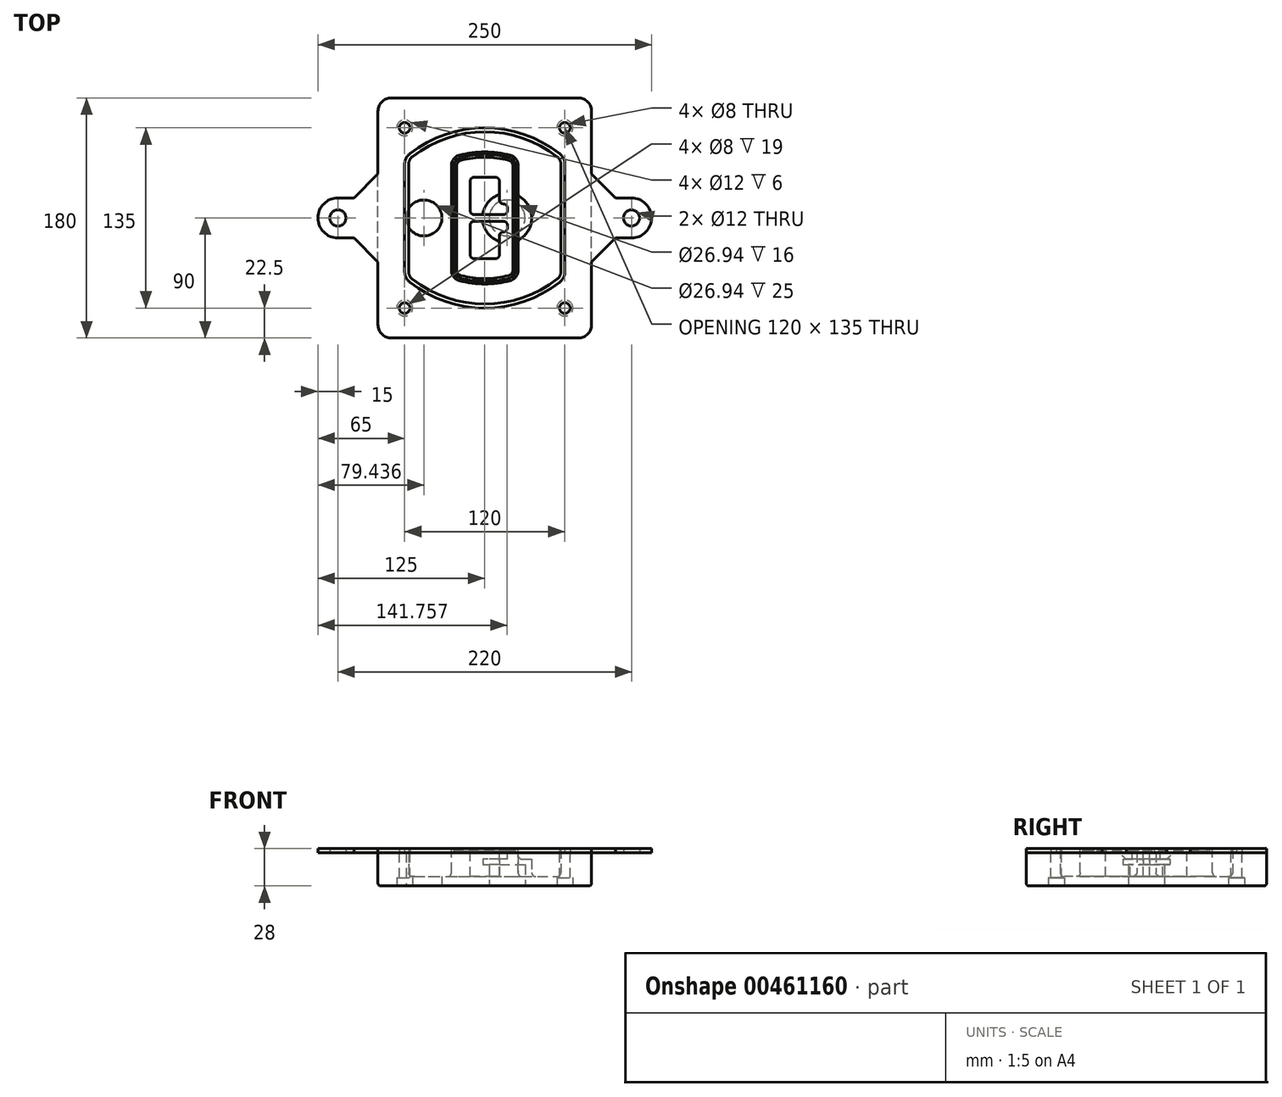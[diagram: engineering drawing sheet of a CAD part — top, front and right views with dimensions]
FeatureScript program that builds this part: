
annotation { "Feature Type Name" : "Feature", "Feature Type Description" : "" }
export const myFeature = defineFeature(function(context is Context, id is Id, definition is map)
    precondition{}
    {
        {
            var Q0;
            Q0=qCreatedBy(makeId("Top.planeOp"),FACE);
            var sketch = newSketch(context, id + "F0", { "sketchPlane" : qUnion([Q0])});
            skPoint(sketch, "E0.rect.middle", {"position": v(0, 0) * mm});
            skLineSegment(sketch, "E1.bottom", {"start": v(-70, -90) * mm, "end": v(70, -90) * mm});
            skLineSegment(sketch, "E1.top", {"start": v(-70, 90) * mm, "end": v(70, 90) * mm});
            skLineSegment(sketch, "E1.left", {"start": v(-80, -80) * mm, "end": v(-80, 80) * mm});
            skLineSegment(sketch, "E1.right", {"start": v(80, -80) * mm, "end": v(80, 80) * mm});
            skLineSegment(sketch, "E2", {"start": v(-80, 90) * mm, "end": v(80, -90) * mm, "construction": true});
            skLineSegment(sketch, "E3", {"start": v(80, 90) * mm, "end": v(-80, -90) * mm, "construction": true});
            skCircle(sketch, "E4", {"center": v(-60, 67.5) * mm, "radius": 4 * mm});
            skCircle(sketch, "E5", {"center": v(60, 67.5) * mm, "radius": 4 * mm});
            skCircle(sketch, "E6", {"center": v(60, -67.5) * mm, "radius": 4 * mm});
            skCircle(sketch, "E7", {"center": v(-60, -67.5) * mm, "radius": 4 * mm});
            skLineSegment(sketch, "E8", {"start": v(-60, 67.5) * mm, "end": v(60, 67.5) * mm, "construction": true});
            skLineSegment(sketch, "E9", {"start": v(60, 67.5) * mm, "end": v(60, -67.5) * mm, "construction": true});
            skLineSegment(sketch, "E10", {"start": v(60, -67.5) * mm, "end": v(-60, -67.5) * mm, "construction": true});
            skLineSegment(sketch, "E11", {"start": v(-60, -67.5) * mm, "end": v(-60, 67.5) * mm, "construction": true});
            skLineSegment(sketch, "E12", {"start": v(-60, 40.3) * mm, "end": v(-60, -40.3) * mm});
            skLineSegment(sketch, "E13", {"start": v(60, 40.3) * mm, "end": v(60, -40.3) * mm});
            skArc(sketch, "E14", {"start": v(56.15, 48.18) * mm, "mid": v(0, 67.5) * mm, "end": v(-56.15, 48.18) * mm});
            skArc(sketch, "E15", {"start": v(-56.15, -48.18) * mm, "mid": v(0, -67.5) * mm, "end": v(56.15, -48.18) * mm});
            skLineSegment(sketch, "E16", {"start": v(-60, 0) * mm, "end": v(60, 0) * mm, "construction": true});
            skPoint(sketch, "E17.visualSharp", {"position": v(-60, -45) * mm});
            skArc(sketch, "E17.filletArc", {"start": v(-60, -40.3) * mm, "mid": v(-58.99, -44.68) * mm, "end": v(-56.15, -48.18) * mm});
            skPoint(sketch, "E18.visualSharp", {"position": v(-60, 45) * mm});
            skArc(sketch, "E18.filletArc", {"start": v(-56.15, 48.18) * mm, "mid": v(-58.99, 44.68) * mm, "end": v(-60, 40.3) * mm});
            skPoint(sketch, "E19.visualSharp", {"position": v(60, 45) * mm});
            skArc(sketch, "E19.filletArc", {"start": v(60, 40.3) * mm, "mid": v(58.99, 44.68) * mm, "end": v(56.15, 48.18) * mm});
            skPoint(sketch, "E20.visualSharp", {"position": v(60, -45) * mm});
            skArc(sketch, "E20.filletArc", {"start": v(56.15, -48.18) * mm, "mid": v(58.99, -44.68) * mm, "end": v(60, -40.3) * mm});
            skPoint(sketch, "E21.visualSharp", {"position": v(-80, 90) * mm});
            skArc(sketch, "E21.filletArc", {"start": v(-70, 90) * mm, "mid": v(-77.07, 87.07) * mm, "end": v(-80, 80) * mm});
            skPoint(sketch, "E22.visualSharp", {"position": v(80, 90) * mm});
            skArc(sketch, "E22.filletArc", {"start": v(80, 80) * mm, "mid": v(77.07, 87.07) * mm, "end": v(70, 90) * mm});
            skPoint(sketch, "E23.visualSharp", {"position": v(80, -90) * mm});
            skArc(sketch, "E23.filletArc", {"start": v(70, -90) * mm, "mid": v(77.07, -87.07) * mm, "end": v(80, -80) * mm});
            skPoint(sketch, "E24.visualSharp", {"position": v(-80, -90) * mm});
            skArc(sketch, "E24.filletArc", {"start": v(-80, -80) * mm, "mid": v(-77.07, -87.07) * mm, "end": v(-70, -90) * mm});
            skArc(sketch, "E25.0", {"start": v(57, 40.3) * mm, "mid": v(56.3, 43.36) * mm, "end": v(54.3, 45.81) * mm});
            skLineSegment(sketch, "E25.1", {"start": v(57, 40.3) * mm, "end": v(57, -40.3) * mm});
            skArc(sketch, "E25.2", {"start": v(54.3, -45.81) * mm, "mid": v(56.3, -43.36) * mm, "end": v(57, -40.3) * mm});
            skArc(sketch, "E25.3", {"start": v(-54.3, -45.81) * mm, "mid": v(0, -64.5) * mm, "end": v(54.3, -45.81) * mm});
            skArc(sketch, "E25.4", {"start": v(-57, -40.3) * mm, "mid": v(-56.3, -43.36) * mm, "end": v(-54.3, -45.81) * mm});
            skArc(sketch, "E25.5", {"start": v(54.3, 45.81) * mm, "mid": v(0, 64.5) * mm, "end": v(-54.3, 45.81) * mm});
            skLineSegment(sketch, "E25.6", {"start": v(-57, 40.3) * mm, "end": v(-57, -40.3) * mm});
            skArc(sketch, "E25.7", {"start": v(-54.3, 45.81) * mm, "mid": v(-56.3, 43.36) * mm, "end": v(-57, 40.3) * mm});
            skArc(sketch, "E26.0", {"start": v(-58.62, 51.33) * mm, "mid": v(-62.58, 46.43) * mm, "end": v(-64, 40.3) * mm});
            skArc(sketch, "E26.1", {"start": v(58.62, 51.33) * mm, "mid": v(0, 71.5) * mm, "end": v(-58.62, 51.33) * mm});
            skArc(sketch, "E26.2", {"start": v(64, 40.3) * mm, "mid": v(62.58, 46.43) * mm, "end": v(58.62, 51.33) * mm});
            skLineSegment(sketch, "E26.3", {"start": v(64, 40.3) * mm, "end": v(64, -40.3) * mm});
            skArc(sketch, "E26.4", {"start": v(58.62, -51.33) * mm, "mid": v(62.58, -46.43) * mm, "end": v(64, -40.3) * mm});
            skLineSegment(sketch, "E26.5", {"start": v(-64, 40.3) * mm, "end": v(-64, -40.3) * mm});
            skArc(sketch, "E26.6", {"start": v(-58.62, -51.33) * mm, "mid": v(0, -71.5) * mm, "end": v(58.62, -51.33) * mm});
            skArc(sketch, "E26.7", {"start": v(-64, -40.3) * mm, "mid": v(-62.58, -46.43) * mm, "end": v(-58.62, -51.33) * mm});
            skSolve(sketch);
        }
        {
            var Q0;
            Q0=makeQuery(id+"F0.imprint","IMPRINT",FACE,{"disambiguationData":[TD([[makeQuery(id+"F0.imprint","IMPRINT",EDGE,{"derivedFrom":sQuery(id+"F0.wireOp",EDGE,"E1.bottom")}),1.0]])]});
            var Q1;
            Q1=makeQuery(id+"F0.imprint","IMPRINT",FACE,{"disambiguationData":[TD([[makeQuery(id+"F0.imprint","IMPRINT",EDGE,{"derivedFrom":sQuery(id+"F0.wireOp",EDGE,"E12")}),1.0]])]});
            var Q2;
            Q2=makeQuery(id+"F0.imprint","IMPRINT",FACE,{"disambiguationData":[TD([[makeQuery(id+"F0.imprint","IMPRINT",EDGE,{"derivedFrom":sQuery(id+"F0.wireOp",EDGE,"E25.0")}),1.0]])]});
            var Q3;
            Q3=makeQuery(id+"F0.imprint","IMPRINT",FACE,{"disambiguationData":[TD([[makeQuery(id+"F0.imprint","IMPRINT",EDGE,{"derivedFrom":sQuery(id+"F0.wireOp",EDGE,"E12")}),-1.0]])]});
            extrude(context, id + "F1", {"entities" : qUnion([Q0, Q1, Q2, Q3]), "oppositeDirection" : true, "depth" : 25 * mm});
        }
        {
            var Q0;
            Q0=makeQuery(id+"F0.imprint","IMPRINT",FACE,{"disambiguationData":[TD([[makeQuery(id+"F0.imprint","IMPRINT",EDGE,{"derivedFrom":sQuery(id+"F0.wireOp",EDGE,"E12")}),1.0]])]});
            extrude(context, id + "F2", {"entities" : qUnion([Q0]), "operationType" : NewBodyOperationType.ADD, "depth" : 3 * mm});
        }
        {
            var Q0;
            Q0=makeQuery(id+"F0.imprint","IMPRINT",FACE,{"disambiguationData":[TD([[makeQuery(id+"F0.imprint","IMPRINT",EDGE,{"derivedFrom":sQuery(id+"F0.wireOp",EDGE,"E25.0")}),1.0]])]});
            extrude(context, id + "F3", {"entities" : qUnion([Q0]), "operationType" : NewBodyOperationType.REMOVE, "oppositeDirection" : true, "depth" : 18 * mm});
        }
        {
            var Q0;
            Q0=makeQuery(id+"F2.opExtrude","CAP_FACE",FACE,{"disambiguationData":[OSD([sQuery(id+"F0.wireOp",EDGE,"E12"),sQuery(id+"F0.wireOp",EDGE,"E13"),sQuery(id+"F0.wireOp",EDGE,"E14"),sQuery(id+"F0.wireOp",EDGE,"E15"),sQuery(id+"F0.wireOp",EDGE,"E17.filletArc"),sQuery(id+"F0.wireOp",EDGE,"E18.filletArc"),sQuery(id+"F0.wireOp",EDGE,"E19.filletArc"),sQuery(id+"F0.wireOp",EDGE,"E20.filletArc"),sQuery(id+"F0.wireOp",EDGE,"E25.0"),sQuery(id+"F0.wireOp",EDGE,"E25.1"),sQuery(id+"F0.wireOp",EDGE,"E25.2"),sQuery(id+"F0.wireOp",EDGE,"E25.3"),sQuery(id+"F0.wireOp",EDGE,"E25.4"),sQuery(id+"F0.wireOp",EDGE,"E25.5"),sQuery(id+"F0.wireOp",EDGE,"E25.6"),sQuery(id+"F0.wireOp",EDGE,"E25.7")])],"isStart":false});
            var sketch = newSketch(context, id + "F4", { "sketchPlane" : qUnion([Q0])});
            skArc(sketch, "E27.0", {"start": v(-19.08, -46.97) * mm, "mid": v(0, -49.5) * mm, "end": v(19.08, -46.97) * mm});
            skArc(sketch, "E28.0", {"start": v(19.08, 46.97) * mm, "mid": v(0, 49.5) * mm, "end": v(-19.08, 46.97) * mm});
            skLineSegment(sketch, "E29", {"start": v(-25, 39.25) * mm, "end": v(-25, -39.25) * mm});
            skLineSegment(sketch, "E30", {"start": v(25, 39.25) * mm, "end": v(25, -39.25) * mm});
            skLineSegment(sketch, "E31", {"start": v(-25, 45.1) * mm, "end": v(25, 45.1) * mm, "construction": true});
            skLineSegment(sketch, "E32", {"start": v(-25, -45.1) * mm, "end": v(25, -45.1) * mm, "construction": true});
            skPoint(sketch, "E33.visualSharp", {"position": v(-25, 45.1) * mm});
            skArc(sketch, "E33.filletArc", {"start": v(-19.08, 46.97) * mm, "mid": v(-23.35, 44.11) * mm, "end": v(-25, 39.25) * mm});
            skPoint(sketch, "E34.visualSharp", {"position": v(25, 45.1) * mm});
            skArc(sketch, "E34.filletArc", {"start": v(25, 39.25) * mm, "mid": v(23.35, 44.11) * mm, "end": v(19.08, 46.97) * mm});
            skPoint(sketch, "E35.visualSharp", {"position": v(25, -45.1) * mm});
            skArc(sketch, "E35.filletArc", {"start": v(19.08, -46.97) * mm, "mid": v(23.35, -44.11) * mm, "end": v(25, -39.25) * mm});
            skPoint(sketch, "E36.visualSharp", {"position": v(-25, -45.1) * mm});
            skArc(sketch, "E36.filletArc", {"start": v(-25, -39.25) * mm, "mid": v(-23.35, -44.11) * mm, "end": v(-19.08, -46.97) * mm});
            skArc(sketch, "E37.0", {"start": v(54.3, 45.81) * mm, "mid": v(0, 64.5) * mm, "end": v(-54.3, 45.81) * mm});
            skArc(sketch, "E37.1", {"start": v(-54.3, 45.81) * mm, "mid": v(-56.3, 43.36) * mm, "end": v(-57, 40.3) * mm});
            skLineSegment(sketch, "E37.2", {"start": v(-57, 40.3) * mm, "end": v(-57, -40.3) * mm});
            skArc(sketch, "E37.3", {"start": v(-57, -40.3) * mm, "mid": v(-56.3, -43.36) * mm, "end": v(-54.3, -45.81) * mm});
            skArc(sketch, "E37.4", {"start": v(-54.3, -45.81) * mm, "mid": v(0, -64.5) * mm, "end": v(54.3, -45.81) * mm});
            skArc(sketch, "E37.5", {"start": v(54.3, -45.81) * mm, "mid": v(56.3, -43.36) * mm, "end": v(57, -40.3) * mm});
            skLineSegment(sketch, "E37.6", {"start": v(57, 40.3) * mm, "end": v(57, -40.3) * mm});
            skArc(sketch, "E37.7", {"start": v(57, 40.3) * mm, "mid": v(56.3, 43.36) * mm, "end": v(54.3, 45.81) * mm});
            skLineSegment(sketch, "E38.0", {"start": v(23, 39.25) * mm, "end": v(23, -39.25) * mm});
            skArc(sketch, "E38.1", {"start": v(18.56, -45.04) * mm, "mid": v(21.76, -42.9) * mm, "end": v(23, -39.25) * mm});
            skArc(sketch, "E38.2", {"start": v(-18.56, -45.04) * mm, "mid": v(0, -47.5) * mm, "end": v(18.56, -45.04) * mm});
            skArc(sketch, "E38.3", {"start": v(-23, -39.25) * mm, "mid": v(-21.76, -42.9) * mm, "end": v(-18.56, -45.04) * mm});
            skLineSegment(sketch, "E38.4", {"start": v(-23, 39.25) * mm, "end": v(-23, -39.25) * mm});
            skArc(sketch, "E38.5", {"start": v(23, 39.25) * mm, "mid": v(21.76, 42.9) * mm, "end": v(18.56, 45.04) * mm});
            skArc(sketch, "E38.6", {"start": v(-18.56, 45.04) * mm, "mid": v(-21.76, 42.9) * mm, "end": v(-23, 39.25) * mm});
            skArc(sketch, "E38.7", {"start": v(18.56, 45.04) * mm, "mid": v(0, 47.5) * mm, "end": v(-18.56, 45.04) * mm});
            skArc(sketch, "E39.0", {"start": v(21, 39.25) * mm, "mid": v(20.18, 41.68) * mm, "end": v(18.04, 43.1) * mm});
            skLineSegment(sketch, "E39.1", {"start": v(21, 39.25) * mm, "end": v(21, -39.25) * mm});
            skArc(sketch, "E39.2", {"start": v(18.04, -43.1) * mm, "mid": v(20.18, -41.68) * mm, "end": v(21, -39.25) * mm});
            skArc(sketch, "E39.3", {"start": v(-18.04, -43.1) * mm, "mid": v(0, -45.5) * mm, "end": v(18.04, -43.1) * mm});
            skArc(sketch, "E39.4", {"start": v(-21, -39.25) * mm, "mid": v(-20.18, -41.68) * mm, "end": v(-18.04, -43.1) * mm});
            skArc(sketch, "E39.5", {"start": v(18.04, 43.1) * mm, "mid": v(0, 45.5) * mm, "end": v(-18.04, 43.1) * mm});
            skLineSegment(sketch, "E39.6", {"start": v(-21, 39.25) * mm, "end": v(-21, -39.25) * mm});
            skArc(sketch, "E39.7", {"start": v(-18.04, 43.1) * mm, "mid": v(-20.18, 41.68) * mm, "end": v(-21, 39.25) * mm});
            skLineSegment(sketch, "E40", {"start": v(-25, 0) * mm, "end": v(25, 0) * mm, "construction": true});
            skLineSegment(sketch, "E41", {"start": v(-11, 5.5) * mm, "end": v(-11, 27.5) * mm});
            skLineSegment(sketch, "E42", {"start": v(-8, 30.5) * mm, "end": v(8, 30.5) * mm});
            skLineSegment(sketch, "E43", {"start": v(11, 27.5) * mm, "end": v(11, 13.5) * mm});
            skLineSegment(sketch, "E44", {"start": v(14, 10.5) * mm, "end": v(14, 10.5) * mm});
            skLineSegment(sketch, "E45", {"start": v(17, 7.5) * mm, "end": v(17, 5.5) * mm});
            skLineSegment(sketch, "E46", {"start": v(14, 2.5) * mm, "end": v(-8, 2.5) * mm});
            skPoint(sketch, "E47.visualSharp", {"position": v(-11, 30.5) * mm});
            skArc(sketch, "E47.filletArc", {"start": v(-8, 30.5) * mm, "mid": v(-10.12, 29.62) * mm, "end": v(-11, 27.5) * mm});
            skPoint(sketch, "E48.visualSharp", {"position": v(11, 30.5) * mm});
            skArc(sketch, "E48.filletArc", {"start": v(11, 27.5) * mm, "mid": v(10.12, 29.62) * mm, "end": v(8, 30.5) * mm});
            skPoint(sketch, "E49.visualSharp", {"position": v(11, 10.5) * mm});
            skArc(sketch, "E49.filletArc", {"start": v(11, 13.5) * mm, "mid": v(11.88, 11.38) * mm, "end": v(14, 10.5) * mm});
            skPoint(sketch, "E50.visualSharp", {"position": v(17, 10.5) * mm});
            skArc(sketch, "E50.filletArc", {"start": v(17, 7.5) * mm, "mid": v(16.12, 9.62) * mm, "end": v(14, 10.5) * mm});
            skPoint(sketch, "E51.visualSharp", {"position": v(17, 2.5) * mm});
            skArc(sketch, "E51.filletArc", {"start": v(14, 2.5) * mm, "mid": v(16.12, 3.38) * mm, "end": v(17, 5.5) * mm});
            skPoint(sketch, "E52.visualSharp", {"position": v(-11, 2.5) * mm});
            skArc(sketch, "E52.filletArc", {"start": v(-11, 5.5) * mm, "mid": v(-10.12, 3.38) * mm, "end": v(-8, 2.5) * mm});
            skLineSegment(sketch, "E53.0.MirrorCS", {"start": v(14, -2.5) * mm, "end": v(-8, -2.5) * mm});
            skArc(sketch, "E54.0.MirrorCS", {"start": v(-11, -5.5) * mm, "mid": v(-10.12, -3.38) * mm, "end": v(-8, -2.5) * mm});
            skLineSegment(sketch, "E55.0.MirrorCS", {"start": v(-11, -5.5) * mm, "end": v(-11, -27.5) * mm});
            skArc(sketch, "E56.0.MirrorCS", {"start": v(-8, -30.5) * mm, "mid": v(-10.12, -29.62) * mm, "end": v(-11, -27.5) * mm});
            skLineSegment(sketch, "E57.0.MirrorCS", {"start": v(-8, -30.5) * mm, "end": v(8, -30.5) * mm});
            skArc(sketch, "E58.0.MirrorCS", {"start": v(11, -27.5) * mm, "mid": v(10.12, -29.62) * mm, "end": v(8, -30.5) * mm});
            skLineSegment(sketch, "E59.0.MirrorCS", {"start": v(11, -27.5) * mm, "end": v(11, -13.5) * mm});
            skArc(sketch, "E60.0.MirrorCS", {"start": v(11, -13.5) * mm, "mid": v(11.88, -11.38) * mm, "end": v(14, -10.5) * mm});
            skArc(sketch, "E61.0.MirrorCS", {"start": v(17, -7.5) * mm, "mid": v(16.12, -9.62) * mm, "end": v(14, -10.5) * mm});
            skLineSegment(sketch, "E62.0.MirrorCS", {"start": v(17, -7.5) * mm, "end": v(17, -5.5) * mm});
            skArc(sketch, "E63.0.MirrorCS", {"start": v(14, -2.5) * mm, "mid": v(16.12, -3.38) * mm, "end": v(17, -5.5) * mm});
            skSolve(sketch);
        }
        {
            var Q0;
            Q0=makeQuery(id+"F4.imprint","IMPRINT",FACE,{"disambiguationData":[TD([[makeQuery(id+"F4.imprint","IMPRINT",EDGE,{"derivedFrom":sQuery(id+"F4.wireOp",EDGE,"E27.0")}),1.0]])]});
            var Q1;
            Q1=makeQuery(id+"F4.imprint","IMPRINT",FACE,{"disambiguationData":[TD([[makeQuery(id+"F4.imprint","IMPRINT",EDGE,{"derivedFrom":sQuery(id+"F4.wireOp",EDGE,"E38.0")}),-1.0]])]});
            var Q2;
            Q2=makeQuery(id+"F4.imprint","IMPRINT",FACE,{"disambiguationData":[TD([[makeQuery(id+"F4.imprint","IMPRINT",EDGE,{"derivedFrom":sQuery(id+"F4.wireOp",EDGE,"E39.0")}),1.0]])]});
            extrude(context, id + "F5", {"entities" : qUnion([Q0, Q1, Q2]), "operationType" : NewBodyOperationType.ADD, "endBound" : BoundingType.UP_TO_NEXT, "oppositeDirection" : true, "depth" : 25 * mm});
        }
        {
            var Q0;
            Q0=makeQuery(id+"F4.imprint","IMPRINT",FACE,{"disambiguationData":[TD([[makeQuery(id+"F4.imprint","IMPRINT",EDGE,{"derivedFrom":sQuery(id+"F4.wireOp",EDGE,"E38.0")}),-1.0]])]});
            extrude(context, id + "F6", {"entities" : qUnion([Q0]), "operationType" : NewBodyOperationType.REMOVE, "oppositeDirection" : true, "depth" : 2 * mm});
        }
        {
            var Q0;
            Q0=makeQuery(id+"F1.opExtrude","CAP_FACE",FACE,{"disambiguationData":[OSD([sQuery(id+"F0.wireOp",EDGE,"E1.bottom"),sQuery(id+"F0.wireOp",EDGE,"E1.top"),sQuery(id+"F0.wireOp",EDGE,"E1.left"),sQuery(id+"F0.wireOp",EDGE,"E1.right"),sQuery(id+"F0.wireOp",EDGE,"E4"),sQuery(id+"F0.wireOp",EDGE,"E5"),sQuery(id+"F0.wireOp",EDGE,"E6"),sQuery(id+"F0.wireOp",EDGE,"E7"),sQuery(id+"F0.wireOp",EDGE,"E21.filletArc"),sQuery(id+"F0.wireOp",EDGE,"E22.filletArc"),sQuery(id+"F0.wireOp",EDGE,"E23.filletArc"),sQuery(id+"F0.wireOp",EDGE,"E24.filletArc")])],"isStart":false});
            var sketch = newSketch(context, id + "F7", { "sketchPlane" : qUnion([Q0])});
            skCircle(sketch, "E64", {"center": v(16.76, 0) * mm, "radius": 13.47 * mm});
            skCircle(sketch, "E65", {"center": v(-45.56, 0) * mm, "radius": 13.47 * mm});
            skLineSegment(sketch, "E66", {"start": v(80, 0) * mm, "end": v(-80, 0) * mm});
            skCircle(sketch, "E67", {"center": v(16.76, 0) * mm, "radius": 18.47 * mm});
            skCircle(sketch, "E68", {"center": v(60, -67.5) * mm, "radius": 6 * mm});
            skCircle(sketch, "E69", {"center": v(-60, -67.5) * mm, "radius": 6 * mm});
            skCircle(sketch, "E70", {"center": v(-60, 67.5) * mm, "radius": 6 * mm});
            skCircle(sketch, "E71", {"center": v(60, 67.5) * mm, "radius": 6 * mm});
            skSolve(sketch);
        }
        {
            var Q0;
            {var subQ1=sQuery(id+"F7.wireOp",EDGE,"E66");var subQ4=sQuery(id+"F7.wireOp",EDGE,"E64");var subQ6=makeQuery(id+"F7.imprint","INTERSECT",VERTEX,{"disambiguationData":[OD(0.0)],"derivedFrom":[subQ4,subQ1]});Q0=makeQuery(id+"F7.imprint","IMPRINT",FACE,{"disambiguationData":[TD([[makeQuery(id+"F7.imprint","IMPRINT",EDGE,{"disambiguationData":[TD([[subQ6,-1.0]])],"derivedFrom":subQ4}),-1.0]])]});}
            var Q1;
            {var subQ0=sQuery(id+"F7.wireOp",EDGE,"E66");var subQ1=sQuery(id+"F7.wireOp",EDGE,"E64");var subQ3=makeQuery(id+"F7.imprint","INTERSECT",VERTEX,{"disambiguationData":[OD(0.0)],"derivedFrom":[subQ1,subQ0]});Q1=makeQuery(id+"F7.imprint","IMPRINT",FACE,{"disambiguationData":[TD([[makeQuery(id+"F7.imprint","IMPRINT",EDGE,{"disambiguationData":[TD([[subQ3,-1.0]])],"derivedFrom":subQ1}),1.0]])]});}
            var Q2;
            {var subQ0=sQuery(id+"F7.wireOp",EDGE,"E66");var subQ1=sQuery(id+"F7.wireOp",EDGE,"E64");var subQ3=makeQuery(id+"F7.imprint","INTERSECT",VERTEX,{"disambiguationData":[OD(0.0)],"derivedFrom":[subQ1,subQ0]});Q2=makeQuery(id+"F7.imprint","IMPRINT",FACE,{"disambiguationData":[TD([[makeQuery(id+"F7.imprint","IMPRINT",EDGE,{"disambiguationData":[TD([[subQ3,1.0]])],"derivedFrom":subQ1}),1.0]])]});}
            var Q3;
            {var subQ1=sQuery(id+"F7.wireOp",EDGE,"E66");var subQ4=sQuery(id+"F7.wireOp",EDGE,"E64");var subQ6=makeQuery(id+"F7.imprint","INTERSECT",VERTEX,{"disambiguationData":[OD(0.0)],"derivedFrom":[subQ4,subQ1]});Q3=makeQuery(id+"F7.imprint","IMPRINT",FACE,{"disambiguationData":[TD([[makeQuery(id+"F7.imprint","IMPRINT",EDGE,{"disambiguationData":[TD([[subQ6,1.0]])],"derivedFrom":subQ4}),-1.0]])]});}
            extrude(context, id + "F8", {"entities" : qUnion([Q0, Q1, Q2, Q3]), "operationType" : NewBodyOperationType.ADD, "oppositeDirection" : true, "depth" : 20 * mm});
        }
        {
            var Q0;
            {var subQ0=sQuery(id+"F7.wireOp",EDGE,"E66");var subQ1=sQuery(id+"F7.wireOp",EDGE,"E64");var subQ3=makeQuery(id+"F7.imprint","INTERSECT",VERTEX,{"disambiguationData":[OD(0.0)],"derivedFrom":[subQ1,subQ0]});Q0=makeQuery(id+"F7.imprint","IMPRINT",FACE,{"disambiguationData":[TD([[makeQuery(id+"F7.imprint","IMPRINT",EDGE,{"disambiguationData":[TD([[subQ3,-1.0]])],"derivedFrom":subQ1}),1.0]])]});}
            var Q1;
            {var subQ0=sQuery(id+"F7.wireOp",EDGE,"E66");var subQ1=sQuery(id+"F7.wireOp",EDGE,"E64");var subQ3=makeQuery(id+"F7.imprint","INTERSECT",VERTEX,{"disambiguationData":[OD(0.0)],"derivedFrom":[subQ1,subQ0]});Q1=makeQuery(id+"F7.imprint","IMPRINT",FACE,{"disambiguationData":[TD([[makeQuery(id+"F7.imprint","IMPRINT",EDGE,{"disambiguationData":[TD([[subQ3,1.0]])],"derivedFrom":subQ1}),1.0]])]});}
            extrude(context, id + "F9", {"entities" : qUnion([Q0, Q1]), "operationType" : NewBodyOperationType.REMOVE, "oppositeDirection" : true, "depth" : 16 * mm});
        }
        {
            var Q0;
            {var subQ0=sQuery(id+"F7.wireOp",EDGE,"E66");var subQ1=sQuery(id+"F7.wireOp",EDGE,"E65");var subQ3=makeQuery(id+"F7.imprint","INTERSECT",VERTEX,{"disambiguationData":[OD(0.0)],"derivedFrom":[subQ1,subQ0]});Q0=makeQuery(id+"F7.imprint","IMPRINT",FACE,{"disambiguationData":[TD([[makeQuery(id+"F7.imprint","IMPRINT",EDGE,{"disambiguationData":[TD([[subQ3,-1.0]])],"derivedFrom":subQ1}),1.0]])]});}
            var Q1;
            {var subQ0=sQuery(id+"F7.wireOp",EDGE,"E66");var subQ1=sQuery(id+"F7.wireOp",EDGE,"E65");var subQ3=makeQuery(id+"F7.imprint","INTERSECT",VERTEX,{"disambiguationData":[OD(0.0)],"derivedFrom":[subQ1,subQ0]});Q1=makeQuery(id+"F7.imprint","IMPRINT",FACE,{"disambiguationData":[TD([[makeQuery(id+"F7.imprint","IMPRINT",EDGE,{"disambiguationData":[TD([[subQ3,1.0]])],"derivedFrom":subQ1}),1.0]])]});}
            extrude(context, id + "F10", {"entities" : qUnion([Q0, Q1]), "operationType" : NewBodyOperationType.REMOVE, "oppositeDirection" : true, "depth" : 25 * mm});
        }
        {
            var Q0;
            Q0=makeQuery(id+"F7.imprint","IMPRINT",FACE,{"disambiguationData":[TD([[makeQuery(id+"F7.imprint","IMPRINT",EDGE,{"derivedFrom":sQuery(id+"F7.wireOp",EDGE,"E68")}),1.0]])]});
            var Q1;
            Q1=makeQuery(id+"F7.imprint","IMPRINT",FACE,{"disambiguationData":[TD([[makeQuery(id+"F7.imprint","IMPRINT",EDGE,{"derivedFrom":makeQuery(id+"F1.opExtrude","CAP_EDGE",EDGE,{"disambiguationData":[OSD([sQuery(id+"F0.wireOp",EDGE,"E5")])],"isStart":false})}),-1.0]])]});
            var Q2;
            Q2=makeQuery(id+"F7.imprint","IMPRINT",FACE,{"disambiguationData":[TD([[makeQuery(id+"F7.imprint","IMPRINT",EDGE,{"derivedFrom":sQuery(id+"F7.wireOp",EDGE,"E69")}),1.0]])]});
            var Q3;
            Q3=makeQuery(id+"F7.imprint","IMPRINT",FACE,{"disambiguationData":[TD([[makeQuery(id+"F7.imprint","IMPRINT",EDGE,{"derivedFrom":makeQuery(id+"F1.opExtrude","CAP_EDGE",EDGE,{"disambiguationData":[OSD([sQuery(id+"F0.wireOp",EDGE,"E4")])],"isStart":false})}),-1.0]])]});
            var Q4;
            Q4=makeQuery(id+"F7.imprint","IMPRINT",FACE,{"disambiguationData":[TD([[makeQuery(id+"F7.imprint","IMPRINT",EDGE,{"derivedFrom":sQuery(id+"F7.wireOp",EDGE,"E70")}),1.0]])]});
            var Q5;
            Q5=makeQuery(id+"F7.imprint","IMPRINT",FACE,{"disambiguationData":[TD([[makeQuery(id+"F7.imprint","IMPRINT",EDGE,{"derivedFrom":makeQuery(id+"F1.opExtrude","CAP_EDGE",EDGE,{"disambiguationData":[OSD([sQuery(id+"F0.wireOp",EDGE,"E7")])],"isStart":false})}),-1.0]])]});
            var Q6;
            Q6=makeQuery(id+"F7.imprint","IMPRINT",FACE,{"disambiguationData":[TD([[makeQuery(id+"F7.imprint","IMPRINT",EDGE,{"derivedFrom":sQuery(id+"F7.wireOp",EDGE,"E71")}),1.0]])]});
            var Q7;
            Q7=makeQuery(id+"F7.imprint","IMPRINT",FACE,{"disambiguationData":[TD([[makeQuery(id+"F7.imprint","IMPRINT",EDGE,{"derivedFrom":makeQuery(id+"F1.opExtrude","CAP_EDGE",EDGE,{"disambiguationData":[OSD([sQuery(id+"F0.wireOp",EDGE,"E6")])],"isStart":false})}),-1.0]])]});
            extrude(context, id + "F11", {"entities" : qUnion([Q0, Q1, Q2, Q3, Q4, Q5, Q6, Q7]), "operationType" : NewBodyOperationType.REMOVE, "oppositeDirection" : true, "depth" : 6 * mm});
        }
        {
            var Q0;
            Q0=makeQuery(id+"F9.boolean.opBoolean","COPY",FACE,{"derivedFrom":makeQuery(id+"F9.opExtrude","CAP_FACE",FACE,{"disambiguationData":[OSD([sQuery(id+"F7.wireOp",EDGE,"E64")])],"isStart":false})});
            var sketch = newSketch(context, id + "F12", { "sketchPlane" : qUnion([Q0])});
            skArc(sketch, "E72.0", {"start": v(11, 17.55) * mm, "mid": v(2.57, 11.82) * mm, "end": v(-1.54, 2.5) * mm});
            skArc(sketch, "E72.1", {"start": v(-1.54, -2.5) * mm, "mid": v(2.57, -11.82) * mm, "end": v(11, -17.55) * mm});
            skLineSegment(sketch, "E73", {"start": v(-1.54, -2.5) * mm, "end": v(14, -2.5) * mm});
            skLineSegment(sketch, "E74.0", {"start": v(14, 2.5) * mm, "end": v(-1.54, 2.5) * mm});
            skArc(sketch, "E74.1", {"start": v(14, 2.5) * mm, "mid": v(16.12, 3.38) * mm, "end": v(17, 5.5) * mm});
            skLineSegment(sketch, "E74.2", {"start": v(17, 7.5) * mm, "end": v(17, 5.5) * mm});
            skArc(sketch, "E74.3", {"start": v(17, 7.5) * mm, "mid": v(16.12, 9.62) * mm, "end": v(14, 10.5) * mm});
            skArc(sketch, "E74.4", {"start": v(11, 13.5) * mm, "mid": v(11.88, 11.38) * mm, "end": v(14, 10.5) * mm});
            skLineSegment(sketch, "E74.5", {"start": v(11, 17.55) * mm, "end": v(11, 13.5) * mm});
            skLineSegment(sketch, "E74.7", {"start": v(14, -2.5) * mm, "end": v(-1.54, -2.5) * mm});
            skArc(sketch, "E74.8", {"start": v(14, -2.5) * mm, "mid": v(16.12, -3.38) * mm, "end": v(17, -5.5) * mm});
            skLineSegment(sketch, "E74.9", {"start": v(17, -7.5) * mm, "end": v(17, -5.5) * mm});
            skArc(sketch, "E74.10", {"start": v(17, -7.5) * mm, "mid": v(16.12, -9.62) * mm, "end": v(14, -10.5) * mm});
            skArc(sketch, "E74.11", {"start": v(11, -13.5) * mm, "mid": v(11.88, -11.38) * mm, "end": v(14, -10.5) * mm});
            skLineSegment(sketch, "E74.12", {"start": v(11, -17.55) * mm, "end": v(11, -13.5) * mm});
            skPoint(sketch, "E75.orphan", {"position": v(11, -27.5) * mm});
            skPoint(sketch, "E76.orphan", {"position": v(-8, -2.5) * mm});
            skPoint(sketch, "E77.orphan", {"position": v(-8, 2.5) * mm});
            skPoint(sketch, "E78.orphan", {"position": v(11, 27.5) * mm});
            skSolve(sketch);
        }
        {
            var Q0;
            {var subQ7=sQuery(id+"F12.wireOp",EDGE,"E72.0");var subQ14=sQuery(id+"F12.wireOp",EDGE,"E72.1");var subQ16=sQuery(id+"F12.wireOp",EDGE,"E74.1");var subQ18=sQuery(id+"F12.wireOp",EDGE,"E74.8");Q0=qUnion([makeQuery(id+"F12.imprint","IMPRINT",FACE,{"disambiguationData":[TD([[makeQuery(id+"F12.imprint","IMPRINT",EDGE,{"derivedFrom":subQ7}),1.0]])]}),makeQuery(id+"F12.imprint","IMPRINT",FACE,{"disambiguationData":[TD([[makeQuery(id+"F12.imprint","IMPRINT",EDGE,{"derivedFrom":subQ14}),1.0]])]}),makeQuery(id+"F12.imprint","IMPRINT",FACE,{"disambiguationData":[TD([[makeQuery(id+"F12.imprint","IMPRINT",EDGE,{"derivedFrom":subQ16}),1.0]])]}),makeQuery(id+"F12.imprint","IMPRINT",FACE,{"disambiguationData":[TD([[makeQuery(id+"F12.imprint","IMPRINT",EDGE,{"derivedFrom":subQ18}),-1.0]])]})]);}
            var Q1;
            Q1=makeQuery(id+"F5.boolean.opBoolean","SPLIT",FACE,{"disambiguationData":[TD([makeQuery(id+"F5.opExtrude","SWEPT_FACE",FACE,{"disambiguationData":[OSD([sQuery(id+"F4.wireOp",EDGE,"E41")])]})])],"derivedFrom":makeQuery(id+"F3.boolean.opBoolean","COPY",FACE,{"derivedFrom":makeQuery(id+"F3.opExtrude","CAP_FACE",FACE,{"disambiguationData":[OSD([sQuery(id+"F0.wireOp",EDGE,"E25.0"),sQuery(id+"F0.wireOp",EDGE,"E25.1"),sQuery(id+"F0.wireOp",EDGE,"E25.2"),sQuery(id+"F0.wireOp",EDGE,"E25.3"),sQuery(id+"F0.wireOp",EDGE,"E25.4"),sQuery(id+"F0.wireOp",EDGE,"E25.5"),sQuery(id+"F0.wireOp",EDGE,"E25.6"),sQuery(id+"F0.wireOp",EDGE,"E25.7")])],"isStart":false})})});
            extrude(context, id + "F13", {"entities" : qUnion([Q0]), "operationType" : NewBodyOperationType.REMOVE, "endBound" : BoundingType.UP_TO_SURFACE, "endBoundEntityFace" : qUnion([Q1]), "depth" : 25 * mm});
        }
        {
            var Q0;
            Q0=makeQuery(id+"F3.boolean.opBoolean","COPY",EDGE,{"derivedFrom":makeQuery(id+"F3.opExtrude","CAP_EDGE",EDGE,{"disambiguationData":[OSD([sQuery(id+"F0.wireOp",EDGE,"E25.6")])],"isStart":false})});
            var Q1;
            Q1=makeQuery(id+"F8.boolean.opBoolean","INTERSECT",EDGE,{"derivedFrom":[makeQuery(id+"F5.opExtrude","SWEPT_FACE",FACE,{"disambiguationData":[OSD([sQuery(id+"F4.wireOp",EDGE,"E30")])]}),makeQuery(id+"F8.opExtrude","CAP_FACE",FACE,{"disambiguationData":[OSD([sQuery(id+"F7.wireOp",EDGE,"E67")])],"isStart":false})]});
            var Q2;
            Q2=makeQuery(id+"F8.boolean.opBoolean","INTERSECT",EDGE,{"disambiguationData":[OD(1.0)],"derivedFrom":[makeQuery(id+"F5.opExtrude","SWEPT_FACE",FACE,{"disambiguationData":[OSD([sQuery(id+"F4.wireOp",EDGE,"E30")])]}),makeQuery(id+"F8.opExtrude","SWEPT_FACE",FACE,{"disambiguationData":[OSD([sQuery(id+"F7.wireOp",EDGE,"E67")])]})]});
            var Q3;
            {var subQ0=sQuery(id+"F4.wireOp",EDGE,"E30");Q3=makeQuery(id+"F8.boolean.opBoolean","SPLIT",EDGE,{"disambiguationData":[TD([makeQuery(id+"F5.opExtrude","SWEPT_FACE",FACE,{"disambiguationData":[OSD([sQuery(id+"F4.wireOp",EDGE,"E35.filletArc")])]})])],"derivedFrom":makeQuery(id+"F5.opExtrude","CAP_EDGE",EDGE,{"disambiguationData":[OSD([subQ0])],"isStart":false})});}
            var Q4;
            {var subQ0=sQuery(id+"F0.wireOp",EDGE,"E25.7");var subQ1=sQuery(id+"F0.wireOp",EDGE,"E25.1");var subQ2=sQuery(id+"F0.wireOp",EDGE,"E25.6");var subQ3=sQuery(id+"F0.wireOp",EDGE,"E25.5");var subQ4=sQuery(id+"F0.wireOp",EDGE,"E25.4");var subQ5=sQuery(id+"F0.wireOp",EDGE,"E25.0");var subQ6=sQuery(id+"F0.wireOp",EDGE,"E25.2");var subQ7=sQuery(id+"F0.wireOp",EDGE,"E25.3");Q4=makeQuery(id+"F8.boolean.opBoolean","INTERSECT",EDGE,{"derivedFrom":[makeQuery(id+"F5.boolean.opBoolean","SPLIT",FACE,{"disambiguationData":[TD([makeQuery(id+"F2.opExtrude","SWEPT_FACE",FACE,{"disambiguationData":[OSD([subQ5])]})])],"derivedFrom":makeQuery(id+"F3.boolean.opBoolean","COPY",FACE,{"derivedFrom":makeQuery(id+"F3.opExtrude","CAP_FACE",FACE,{"disambiguationData":[OSD([subQ5,subQ1,subQ6,subQ7,subQ4,subQ3,subQ2,subQ0])],"isStart":false})})}),makeQuery(id+"F8.opExtrude","SWEPT_FACE",FACE,{"disambiguationData":[OSD([sQuery(id+"F7.wireOp",EDGE,"E67")])]})]});}
            var Q5;
            Q5=makeQuery(id+"F8.boolean.opBoolean","INTERSECT",EDGE,{"disambiguationData":[OD(0.0)],"derivedFrom":[makeQuery(id+"F5.opExtrude","SWEPT_FACE",FACE,{"disambiguationData":[OSD([sQuery(id+"F4.wireOp",EDGE,"E30")])]}),makeQuery(id+"F8.opExtrude","SWEPT_FACE",FACE,{"disambiguationData":[OSD([sQuery(id+"F7.wireOp",EDGE,"E67")])]})]});
            fillet(context, id + "F14", {"entities" : qUnion([Q0, Q1, Q2, Q3, Q4, Q5]), "radius" : 3 * mm, "tangentPropagation" : true, "allowEdgeOverflow" : false});
        }
        {
            var Q0;
            Q0=makeQuery(id+"F1.opExtrude","CAP_EDGE",EDGE,{"disambiguationData":[OSD([sQuery(id+"F0.wireOp",EDGE,"E1.bottom")])],"isStart":false});
            fillet(context, id + "F15", {"entities" : qUnion([Q0]), "radius" : 2 * mm, "tangentPropagation" : true, "allowEdgeOverflow" : false});
        }
        {
            var Q0;
            {var subQ0=sQuery(id+"F0.wireOp",EDGE,"E21.filletArc");var subQ1=sQuery(id+"F0.wireOp",EDGE,"E7");var subQ2=sQuery(id+"F0.wireOp",EDGE,"E6");var subQ3=sQuery(id+"F0.wireOp",EDGE,"E5");var subQ4=sQuery(id+"F0.wireOp",EDGE,"E4");var subQ5=sQuery(id+"F0.wireOp",EDGE,"E22.filletArc");var subQ6=sQuery(id+"F0.wireOp",EDGE,"E1.bottom");var subQ7=sQuery(id+"F0.wireOp",EDGE,"E1.right");var subQ8=sQuery(id+"F0.wireOp",EDGE,"E1.top");var subQ9=sQuery(id+"F0.wireOp",EDGE,"E1.left");var subQ10=sQuery(id+"F0.wireOp",EDGE,"E23.filletArc");var subQ11=sQuery(id+"F0.wireOp",EDGE,"E24.filletArc");Q0=makeQuery(id+"F2.boolean.opBoolean","SPLIT",FACE,{"disambiguationData":[TD([makeQuery(id+"F1.opExtrude","SWEPT_FACE",FACE,{"disambiguationData":[OSD([subQ6])]})])],"derivedFrom":makeQuery(id+"F1.opExtrude","CAP_FACE",FACE,{"disambiguationData":[OSD([subQ6,subQ8,subQ9,subQ7,subQ4,subQ3,subQ2,subQ1,subQ0,subQ5,subQ10,subQ11])],"isStart":true})});}
            var sketch = newSketch(context, id + "F16", { "sketchPlane" : qUnion([Q0])});
            skPoint(sketch, "E79.endSnap0", {"position": v(0, -90) * mm});
            skArc(sketch, "E80.0", {"start": v(56.15, 48.18) * mm, "mid": v(0, 67.5) * mm, "end": v(-56.15, 48.18) * mm});
            skArc(sketch, "E80.1", {"start": v(60, 40.3) * mm, "mid": v(58.99, 44.68) * mm, "end": v(56.15, 48.18) * mm});
            skLineSegment(sketch, "E80.2", {"start": v(60, 40.3) * mm, "end": v(60, -40.3) * mm});
            skArc(sketch, "E80.3", {"start": v(-56.15, -48.18) * mm, "mid": v(0, -67.5) * mm, "end": v(56.15, -48.18) * mm});
            skArc(sketch, "E80.4", {"start": v(56.15, -48.18) * mm, "mid": v(58.99, -44.68) * mm, "end": v(60, -40.3) * mm});
            skLineSegment(sketch, "E80.5", {"start": v(-60, 40.3) * mm, "end": v(-60, -40.3) * mm});
            skCircle(sketch, "E80.6", {"center": v(60, -67.5) * mm, "radius": 4 * mm});
            skCircle(sketch, "E80.7", {"center": v(-60, -67.5) * mm, "radius": 4 * mm});
            skCircle(sketch, "E80.8", {"center": v(-60, 67.5) * mm, "radius": 4 * mm});
            skCircle(sketch, "E80.9", {"center": v(60, 67.5) * mm, "radius": 4 * mm});
            skPoint(sketch, "E80.10", {"position": v(-56.15, 48.18) * mm});
            skArc(sketch, "E80.11", {"start": v(-56.15, 48.18) * mm, "mid": v(-58.99, 44.68) * mm, "end": v(-60, 40.3) * mm});
            skArc(sketch, "E80.12", {"start": v(-60, -40.3) * mm, "mid": v(-58.99, -44.68) * mm, "end": v(-56.15, -48.18) * mm});
            skArc(sketch, "E80.13", {"start": v(80, 80) * mm, "mid": v(77.07, 87.07) * mm, "end": v(70, 90) * mm});
            skLineSegment(sketch, "E80.14", {"start": v(80, -80) * mm, "end": v(80, 80) * mm});
            skArc(sketch, "E80.15", {"start": v(70, -90) * mm, "mid": v(77.07, -87.07) * mm, "end": v(80, -80) * mm});
            skLineSegment(sketch, "E80.16", {"start": v(-70, -90) * mm, "end": v(70, -90) * mm});
            skArc(sketch, "E80.17", {"start": v(-80, -80) * mm, "mid": v(-77.07, -87.07) * mm, "end": v(-70, -90) * mm});
            skLineSegment(sketch, "E80.18", {"start": v(-80, -80) * mm, "end": v(-80, 80) * mm});
            skLineSegment(sketch, "E80.19", {"start": v(-70, 90) * mm, "end": v(70, 90) * mm});
            skArc(sketch, "E80.20", {"start": v(-70, 90) * mm, "mid": v(-77.07, 87.07) * mm, "end": v(-80, 80) * mm});
            skPoint(sketch, "E80.21", {"position": v(58.99, -44.68) * mm});
            skPoint(sketch, "E80.22", {"position": v(-58.99, 44.68) * mm});
            skLineSegment(sketch, "E81", {"start": v(80, 0) * mm, "end": v(110, 0) * mm, "construction": true});
            skPoint(sketch, "E81.endSnap0", {"position": v(80, 0) * mm});
            skArc(sketch, "E82", {"start": v(110, -15) * mm, "mid": v(125, 0) * mm, "end": v(110, 15) * mm});
            skLineSegment(sketch, "E83", {"start": v(110, 15) * mm, "end": v(105.34, 15) * mm});
            skLineSegment(sketch, "E84", {"start": v(110, -15) * mm, "end": v(105.34, -15) * mm});
            skCircle(sketch, "E85", {"center": v(110, 0) * mm, "radius": 6 * mm});
            skLineSegment(sketch, "E86", {"start": v(105.34, 15) * mm, "end": v(98, 15) * mm});
            skLineSegment(sketch, "E87", {"start": v(110, -15) * mm, "end": v(98, -15) * mm});
            skLineSegment(sketch, "E88", {"start": v(98, -15) * mm, "end": v(80, -33) * mm});
            skLineSegment(sketch, "E89", {"start": v(98, 15) * mm, "end": v(80, 33) * mm});
            skLineSegment(sketch, "E90", {"start": v(0, 90) * mm, "end": v(0, -90) * mm, "construction": true});
            skLineSegment(sketch, "E91.MirrorCS", {"start": v(-110, -15) * mm, "end": v(-105.34, -15) * mm});
            skLineSegment(sketch, "E92.MirrorCS", {"start": v(-110, 15) * mm, "end": v(-105.34, 15) * mm});
            skArc(sketch, "E93.MirrorCS", {"start": v(-70, -90) * mm, "mid": v(-77.07, -87.07) * mm, "end": v(-80, -80) * mm});
            skArc(sketch, "E94.MirrorCS", {"start": v(-80, 80) * mm, "mid": v(-77.07, 87.07) * mm, "end": v(-70, 90) * mm});
            skLineSegment(sketch, "E95.MirrorCS", {"start": v(-98, -15) * mm, "end": v(-80, -33) * mm});
            skLineSegment(sketch, "E96.MirrorCS", {"start": v(-105.34, 15) * mm, "end": v(-98, 15) * mm});
            skArc(sketch, "E97.MirrorCS", {"start": v(-110, -15) * mm, "mid": v(-125, 0) * mm, "end": v(-110, 15) * mm});
            skLineSegment(sketch, "E98.MirrorCS", {"start": v(-80, 0) * mm, "end": v(-110, 0) * mm, "construction": true});
            skLineSegment(sketch, "E99.MirrorCS", {"start": v(-98, 15) * mm, "end": v(-80, 33) * mm});
            skCircle(sketch, "E100.MirrorC", {"center": v(-110, 0) * mm, "radius": 6 * mm});
            skPoint(sketch, "E101.MirrorP", {"position": v(-80, 0) * mm});
            skLineSegment(sketch, "E102.MirrorCS", {"start": v(-110, -15) * mm, "end": v(-98, -15) * mm});
            skSolve(sketch);
        }
        {
            var Q0;
            {var subQ3=sQuery(id+"F16.wireOp",EDGE,"E95.MirrorCS");Q0=makeQuery(id+"F16.imprint","IMPRINT",FACE,{"disambiguationData":[TD([[makeQuery(id+"F16.imprint","IMPRINT",EDGE,{"derivedFrom":subQ3}),1.0]])]});}
            var Q1;
            Q1=makeQuery(id+"F16.imprint","IMPRINT",FACE,{"disambiguationData":[TD([[makeQuery(id+"F16.imprint","IMPRINT",EDGE,{"derivedFrom":sQuery(id+"F16.wireOp",EDGE,"E80.0")}),-1.0]])]});
            var Q2;
            {var subQ1=sQuery(id+"F16.wireOp",EDGE,"E82");Q2=makeQuery(id+"F16.imprint","IMPRINT",FACE,{"disambiguationData":[TD([[makeQuery(id+"F16.imprint","IMPRINT",EDGE,{"derivedFrom":subQ1}),1.0]])]});}
            var Q3;
            Q3=makeQuery(id+"F2.opExtrude","CAP_FACE",FACE,{"disambiguationData":[OSD([sQuery(id+"F0.wireOp",EDGE,"E12"),sQuery(id+"F0.wireOp",EDGE,"E13"),sQuery(id+"F0.wireOp",EDGE,"E14"),sQuery(id+"F0.wireOp",EDGE,"E15"),sQuery(id+"F0.wireOp",EDGE,"E17.filletArc"),sQuery(id+"F0.wireOp",EDGE,"E18.filletArc"),sQuery(id+"F0.wireOp",EDGE,"E19.filletArc"),sQuery(id+"F0.wireOp",EDGE,"E20.filletArc"),sQuery(id+"F0.wireOp",EDGE,"E25.0"),sQuery(id+"F0.wireOp",EDGE,"E25.1"),sQuery(id+"F0.wireOp",EDGE,"E25.2"),sQuery(id+"F0.wireOp",EDGE,"E25.3"),sQuery(id+"F0.wireOp",EDGE,"E25.4"),sQuery(id+"F0.wireOp",EDGE,"E25.5"),sQuery(id+"F0.wireOp",EDGE,"E25.6"),sQuery(id+"F0.wireOp",EDGE,"E25.7")])],"isStart":false});
            extrude(context, id + "F17", {"entities" : qUnion([Q0, Q1, Q2]), "endBound" : BoundingType.UP_TO_SURFACE, "endBoundEntityFace" : qUnion([Q3]), "depth" : 25 * mm});
        }
    });
